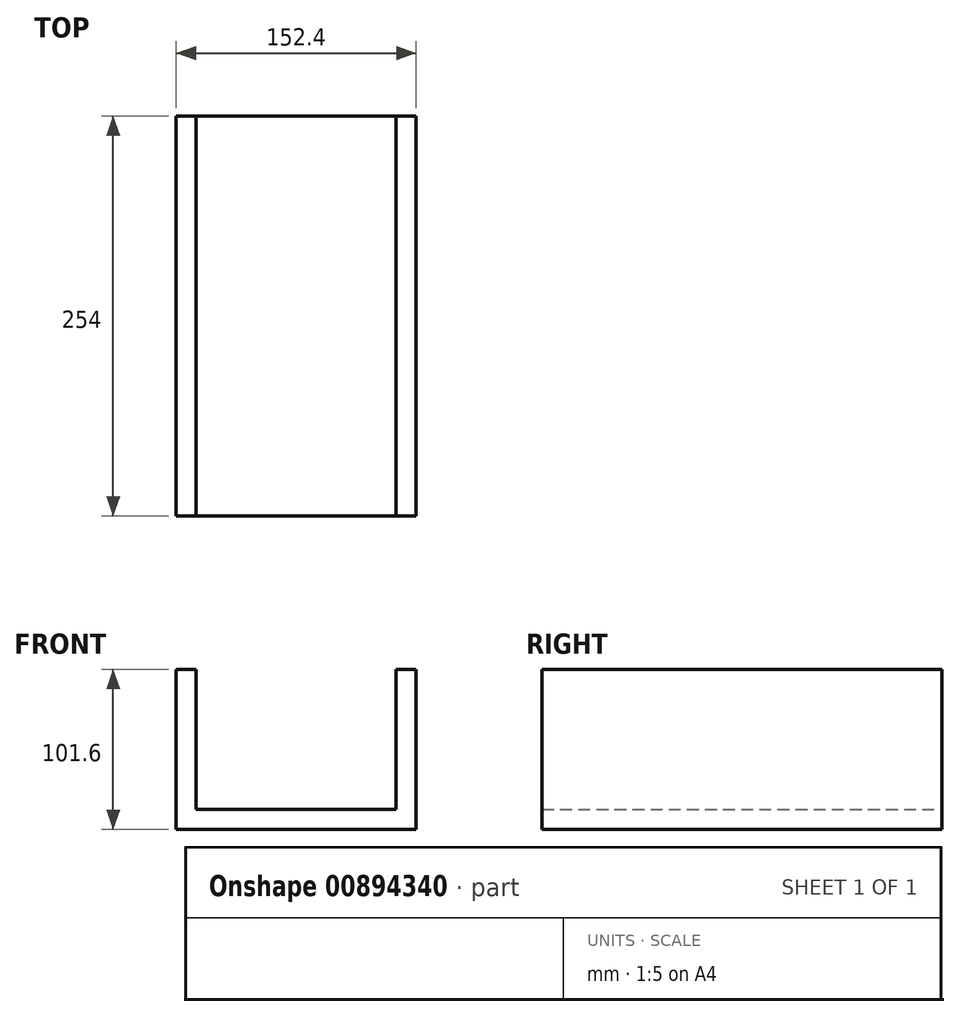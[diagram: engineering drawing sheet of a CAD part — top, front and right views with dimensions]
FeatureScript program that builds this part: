
annotation { "Feature Type Name" : "Feature", "Feature Type Description" : "" }
export const myFeature = defineFeature(function(context is Context, id is Id, definition is map)
    precondition{}
    {
        {
            var Q0;
            Q0=qCreatedBy(makeId("Front.planeOp"),FACE);
            var sketch = newSketch(context, id + "F0", { "sketchPlane" : qUnion([Q0])});
            skLineSegment(sketch, "E0.bottom", {"start": v(-76.2, 0) * mm, "end": v(76.2, 0) * mm});
            skLineSegment(sketch, "E0.top", {"start": v(-76.2, 101.6) * mm, "end": v(-63.5, 101.6) * mm});
            skLineSegment(sketch, "E0.left", {"start": v(-76.2, 0) * mm, "end": v(-76.2, 101.6) * mm});
            skLineSegment(sketch, "E0.right", {"start": v(76.2, 0) * mm, "end": v(76.2, 101.6) * mm});
            skLineSegment(sketch, "E1.top", {"start": v(-63.5, 12.7) * mm, "end": v(63.5, 12.7) * mm});
            skLineSegment(sketch, "E1.left", {"start": v(-63.5, 101.6) * mm, "end": v(-63.5, 12.7) * mm});
            skLineSegment(sketch, "E1.right", {"start": v(63.5, 101.6) * mm, "end": v(63.5, 12.7) * mm});
            skLineSegment(sketch, "E2.trimOffspring", {"start": v(63.5, 101.6) * mm, "end": v(76.2, 101.6) * mm});
            skSolve(sketch);
        }
        {
            var Q0;
            Q0=makeQuery(id+"F0.imprint","IMPRINT",FACE,{"disambiguationData":[TD([[makeQuery(id+"F0.imprint","IMPRINT",EDGE,{"derivedFrom":sQuery(id+"F0.wireOp",EDGE,"E0.bottom")}),1.0]])]});
            extrude(context, id + "F1", {"entities" : qUnion([Q0]), "endBound" : BoundingType.SYMMETRIC, "depth" : 254 * mm, "offsetDistance" : 25.4 * mm});
        }
    });
